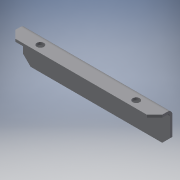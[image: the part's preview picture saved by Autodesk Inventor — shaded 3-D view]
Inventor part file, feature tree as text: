
AUTODESK INVENTOR PART (.ipt)
format: ipt  version: 2016 (Build 200138000, 138)  size: 126,464 bytes
history: native  units: mm
features: sheet_metal_op x4, other x3, sketch x3, reference x3, hole x1
ambient origin geometry x8: Origin, YZ Plane, XZ Plane, XY Plane, X Axis, Y Axis, Z Axis, Center Point
bodies: Solid1 (feature_tree)
feature tree (14):
  sheet_metal_op  "Face1"
  sheet_metal_op  "Flange1"
  other  "Corner Chamfer1"
  hole  "Hole1"  [1 undecoded]
  sketch  "Sketch4"  dims[d3=2.0mm d4=1.0mm d5=4.0mm d6=2.0mm d7=25.0mm d8=90.0deg d9=2.0mm d10=8.0mm d11=2.0mm d12=2.0mm d13=6.0mm d14=6.0mm d15=45.0deg d16=5.5mm d17=6.0mm d18=4.0mm d19=2.0mm d20=90.0deg d21=2.0mm d22=20.594885mm]
  sketch  "Sketch1"  dims[d0=115.0mm d1=14.0mm]
  other  "Plate1"
  sketch  "Sketch2"  dims[d2=2.0mm]
  other  "Plate2"
  sheet_metal_op  "Bend1"
  sheet_metal_op  "Corner1"
  reference  "Reference1"
  reference  "Reference2"
  reference  "Reference3"
note: 1 required parameter value undecoded (feature->parameter linkage not recoverable at this tier; creation-order binding heuristic only, values carry confidence <= 0.55)
